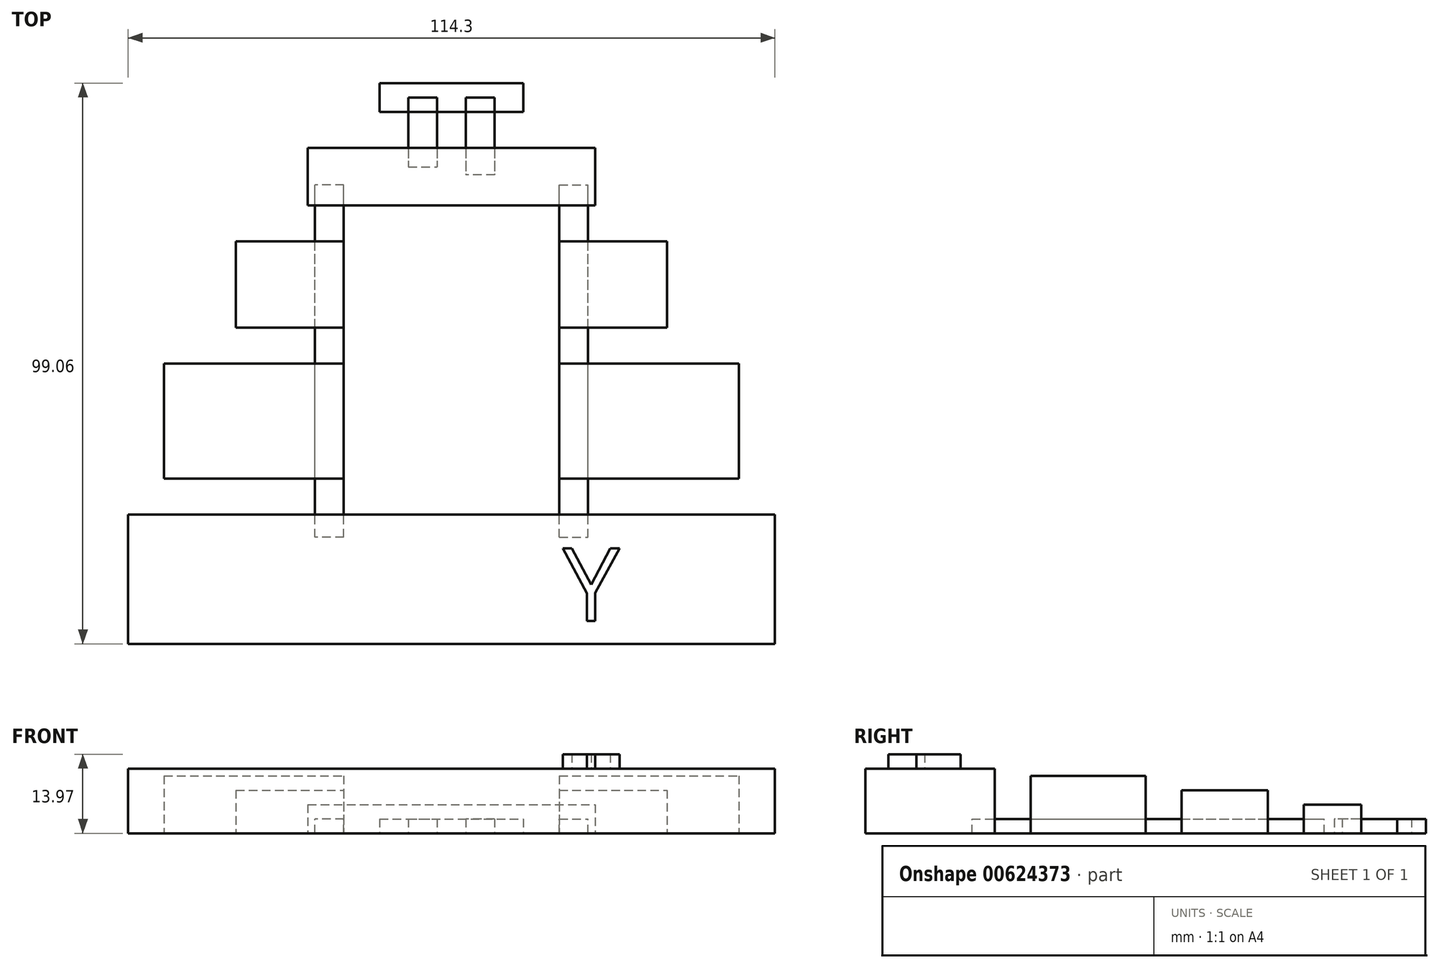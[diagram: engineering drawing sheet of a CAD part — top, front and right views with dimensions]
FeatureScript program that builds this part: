
annotation { "Feature Type Name" : "Feature", "Feature Type Description" : "" }
export const myFeature = defineFeature(function(context is Context, id is Id, definition is map)
    precondition{}
    {
        {
            var Q0;
            Q0=qCreatedBy(makeId("Top.planeOp"),FACE);
            var sketch = newSketch(context, id + "F0", { "sketchPlane" : qUnion([Q0])});
            skLineSegment(sketch, "E0.bottom", {"start": v(-50.8, -42.7) * mm, "end": v(63.5, -42.7) * mm});
            skLineSegment(sketch, "E0.top", {"start": v(-50.8, -65.55) * mm, "end": v(63.5, -65.55) * mm});
            skLineSegment(sketch, "E0.left", {"start": v(-50.8, -42.7) * mm, "end": v(-50.8, -65.55) * mm});
            skLineSegment(sketch, "E0.right", {"start": v(63.5, -42.7) * mm, "end": v(63.5, -65.55) * mm});
            skSolve(sketch);
        }
        {
            var Q0;
            Q0 = qSketchRegion(id + "F0", true);
            extrude(context, id + "F1", {"entities" : qUnion([Q0]), "depth" : 11.43 * mm, "offsetDistance" : 25.4 * mm});
        }
        {
            var Q0;
            Q0=makeQuery(id+"F1.opExtrude","CAP_FACE",FACE,{"disambiguationData":[OSD([sQuery(id+"F0.wireOp",EDGE,"E0.bottom"),sQuery(id+"F0.wireOp",EDGE,"E0.top"),sQuery(id+"F0.wireOp",EDGE,"E0.left"),sQuery(id+"F0.wireOp",EDGE,"E0.right")])],"isStart":false});
            var sketch = newSketch(context, id + "F2", { "sketchPlane" : qUnion([Q0])});
            skText(sketch, "E1", { "text": "Y", "fontName": "OpenSans-Regular.ttf"});
            const initialGuessF2  = {"E1": [0.026, -0.0615, 1, 0, 0.01289]};
            skSetInitialGuess(sketch, initialGuessF2);
            skSolve(sketch);
        }
        {
            var Q0;
            Q0 = qSketchRegion(id + "F2", true);
            extrude(context, id + "F3", {"entities" : qUnion([Q0]), "operationType" : NewBodyOperationType.ADD, "depth" : 2.54 * mm, "offsetDistance" : 25.4 * mm});
        }
        {
            var Q0;
            Q0=qCreatedBy(makeId("Top.planeOp"),FACE);
            var sketch = newSketch(context, id + "F4", { "sketchPlane" : qUnion([Q0])});
            skLineSegment(sketch, "E2.bottom", {"start": v(-44.45, -16.02) * mm, "end": v(57.15, -16.02) * mm});
            skLineSegment(sketch, "E2.top", {"start": v(-44.45, -36.34) * mm, "end": v(57.15, -36.34) * mm});
            skLineSegment(sketch, "E2.left", {"start": v(-44.45, -16.02) * mm, "end": v(-44.45, -36.34) * mm});
            skLineSegment(sketch, "E2.right", {"start": v(57.15, -16.02) * mm, "end": v(57.15, -36.34) * mm});
            skSolve(sketch);
        }
        {
            var Q0;
            Q0=makeQuery(id+"F4.imprint","IMPRINT",FACE,{"disambiguationData":[TD([[makeQuery(id+"F4.imprint","IMPRINT",EDGE,{"derivedFrom":sQuery(id+"F4.wireOp",EDGE,"E2.bottom")}),-1.0]])]});
            extrude(context, id + "F5", {"entities" : qUnion([Q0]), "depth" : 10.16 * mm, "offsetDistance" : 25.4 * mm});
        }
        {
            var Q0;
            Q0=qCreatedBy(makeId("Top.planeOp"),FACE);
            var sketch = newSketch(context, id + "F6", { "sketchPlane" : qUnion([Q0])});
            skLineSegment(sketch, "E3.bottom", {"start": v(-31.75, 5.57) * mm, "end": v(44.45, 5.57) * mm});
            skLineSegment(sketch, "E3.top", {"start": v(-31.75, -9.67) * mm, "end": v(44.45, -9.67) * mm});
            skLineSegment(sketch, "E3.left", {"start": v(-31.75, 5.57) * mm, "end": v(-31.75, -9.67) * mm});
            skLineSegment(sketch, "E3.right", {"start": v(44.45, 5.57) * mm, "end": v(44.45, -9.67) * mm});
            skSolve(sketch);
        }
        {
            var Q0;
            Q0 = qSketchRegion(id + "F6", true);
            extrude(context, id + "F7", {"entities" : qUnion([Q0]), "depth" : 7.62 * mm, "offsetDistance" : 25.4 * mm});
        }
        {
            var Q0;
            Q0=qCreatedBy(makeId("Top.planeOp"),FACE);
            var sketch = newSketch(context, id + "F8", { "sketchPlane" : qUnion([Q0])});
            skLineSegment(sketch, "E4.bottom", {"start": v(-19.05, 22.08) * mm, "end": v(31.75, 22.08) * mm});
            skLineSegment(sketch, "E4.top", {"start": v(-19.05, 11.92) * mm, "end": v(31.75, 11.92) * mm});
            skLineSegment(sketch, "E4.left", {"start": v(-19.05, 22.08) * mm, "end": v(-19.05, 11.92) * mm});
            skLineSegment(sketch, "E4.right", {"start": v(31.75, 22.08) * mm, "end": v(31.75, 11.92) * mm});
            skSolve(sketch);
        }
        {
            var Q0;
            Q0=makeQuery(id+"F8.imprint","IMPRINT",FACE,{"disambiguationData":[TD([[makeQuery(id+"F8.imprint","IMPRINT",EDGE,{"derivedFrom":sQuery(id+"F8.wireOp",EDGE,"E4.bottom")}),-1.0]])]});
            extrude(context, id + "F9", {"entities" : qUnion([Q0]), "depth" : 5.08 * mm, "offsetDistance" : 25.4 * mm});
        }
        {
            var Q0;
            Q0=qCreatedBy(makeId("Top.planeOp"),FACE);
            var sketch = newSketch(context, id + "F10", { "sketchPlane" : qUnion([Q0])});
            skLineSegment(sketch, "E5.bottom", {"start": v(-6.35, 33.5) * mm, "end": v(19.05, 33.5) * mm});
            skLineSegment(sketch, "E5.top", {"start": v(-6.35, 28.43) * mm, "end": v(19.05, 28.43) * mm});
            skLineSegment(sketch, "E5.left", {"start": v(-6.35, 33.5) * mm, "end": v(-6.35, 28.43) * mm});
            skLineSegment(sketch, "E5.right", {"start": v(19.05, 33.5) * mm, "end": v(19.05, 28.43) * mm});
            skSolve(sketch);
        }
        {
            var Q0;
            Q0=makeQuery(id+"F10.imprint","IMPRINT",FACE,{"disambiguationData":[TD([[makeQuery(id+"F10.imprint","IMPRINT",EDGE,{"derivedFrom":sQuery(id+"F10.wireOp",EDGE,"E5.bottom")}),-1.0]])]});
            extrude(context, id + "F11", {"entities" : qUnion([Q0]), "depth" : 2.54 * mm, "offsetDistance" : 25.4 * mm});
        }
        {
            var Q0;
            Q0=qCreatedBy(makeId("Top.planeOp"),FACE);
            var sketch = newSketch(context, id + "F12", { "sketchPlane" : qUnion([Q0])});
            skLineSegment(sketch, "E6.bottom", {"start": v(-1.27, 30.93) * mm, "end": v(3.8, 30.93) * mm});
            skLineSegment(sketch, "E6.top", {"start": v(-1.27, 18.68) * mm, "end": v(3.8, 18.68) * mm});
            skLineSegment(sketch, "E6.left", {"start": v(-1.27, 30.93) * mm, "end": v(-1.27, 18.68) * mm});
            skLineSegment(sketch, "E6.right", {"start": v(3.8, 30.93) * mm, "end": v(3.8, 18.68) * mm});
            skLineSegment(sketch, "E7.bottom", {"start": v(13.97, 30.93) * mm, "end": v(8.89, 30.93) * mm});
            skLineSegment(sketch, "E7.top", {"start": v(13.97, 17.29) * mm, "end": v(8.89, 17.29) * mm});
            skLineSegment(sketch, "E7.left", {"start": v(13.97, 30.93) * mm, "end": v(13.97, 17.29) * mm});
            skLineSegment(sketch, "E7.right", {"start": v(8.89, 30.93) * mm, "end": v(8.89, 17.29) * mm});
            skSolve(sketch);
        }
        {
            var Q0;
            Q0 = qSketchRegion(id + "F12", true);
            extrude(context, id + "F13", {"entities" : qUnion([Q0]), "depth" : 2.54 * mm, "offsetDistance" : 25.4 * mm});
        }
        {
            var Q0;
            Q0=qCreatedBy(makeId("Front.planeOp"),FACE);
            var sketch = newSketch(context, id + "F14", { "sketchPlane" : qUnion([Q0])});
            skLineSegment(sketch, "E8.0", {"start": v(-50.8, 0) * mm, "end": v(63.5, 0) * mm, "construction": true});
            skLineSegment(sketch, "E9.bottom", {"start": v(25.4, 0) * mm, "end": v(30.48, 0) * mm});
            skLineSegment(sketch, "E9.top", {"start": v(25.4, 2.54) * mm, "end": v(30.48, 2.54) * mm});
            skLineSegment(sketch, "E9.left", {"start": v(25.4, 0) * mm, "end": v(25.4, 2.54) * mm});
            skLineSegment(sketch, "E9.right", {"start": v(30.48, 0) * mm, "end": v(30.48, 2.54) * mm});
            skPoint(sketch, "E10", {"position": v(6.35, 0) * mm});
            skLineSegment(sketch, "E11", {"start": v(6.35, 0) * mm, "end": v(6.35, 10.63) * mm, "construction": true});
            skLineSegment(sketch, "E12.MirrorCS", {"start": v(-17.78, 0) * mm, "end": v(-17.78, 2.54) * mm});
            skLineSegment(sketch, "E13.MirrorCS", {"start": v(-12.7, 2.54) * mm, "end": v(-17.78, 2.54) * mm});
            skLineSegment(sketch, "E14.MirrorCS", {"start": v(-12.7, 0) * mm, "end": v(-17.78, 0) * mm});
            skLineSegment(sketch, "E15.MirrorCS", {"start": v(-12.7, 0) * mm, "end": v(-12.7, 2.54) * mm});
            skSolve(sketch);
        }
        {
            var Q0;
            Q0 = qSketchRegion(id + "F14", true);
            extrude(context, id + "F15", {"entities" : qUnion([Q0]), "depth" : 46.74 * mm, "offsetDistance" : 25.4 * mm, "hasSecondDirection" : true, "secondDirectionOppositeDirection" : true, "secondDirectionDepth" : 15.5 * mm});
        }
        {
            var Q0;
            Q0=qCreatedBy(makeId("Top.planeOp"),FACE);
            var sketch = newSketch(context, id + "F16", { "sketchPlane" : qUnion([Q0])});
            skLineSegment(sketch, "E16.0.0", {"start": v(-44.45, -16.02) * mm, "end": v(-44.45, -36.34) * mm, "construction": true});
            skLineSegment(sketch, "E16.0.1", {"start": v(-44.45, -36.34) * mm, "end": v(57.15, -36.34) * mm, "construction": true});
            skLineSegment(sketch, "E16.0.2", {"start": v(57.15, -36.34) * mm, "end": v(57.15, -16.02) * mm, "construction": true});
            skLineSegment(sketch, "E16.0.3", {"start": v(57.15, -16.02) * mm, "end": v(-44.45, -16.02) * mm, "construction": true});
            skPoint(sketch, "E17.0", {"position": v(25.4, -15.62) * mm});
            skPoint(sketch, "E18.0", {"position": v(-12.7, -15.62) * mm});
            skLineSegment(sketch, "E19.bottom", {"start": v(25.4, 9.38) * mm, "end": v(-12.7, 9.38) * mm});
            skLineSegment(sketch, "E19.top", {"start": v(25.4, -41.42) * mm, "end": v(-12.7, -41.42) * mm});
            skLineSegment(sketch, "E19.left", {"start": v(25.4, 9.38) * mm, "end": v(25.4, -41.42) * mm});
            skLineSegment(sketch, "E19.right", {"start": v(-12.7, 9.38) * mm, "end": v(-12.7, -41.42) * mm});
            skPoint(sketch, "E19.middle", {"position": v(6.35, -16.02) * mm});
            skSolve(sketch);
        }
        {
            var Q0;
            Q0 = qSketchRegion(id + "F16", true);
            extrude(context, id + "F17", {"entities" : qUnion([Q0]), "operationType" : NewBodyOperationType.REMOVE, "depth" : 25.4 * mm, "offsetDistance" : 25.4 * mm});
        }
    });
